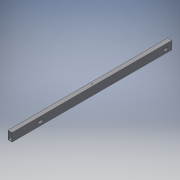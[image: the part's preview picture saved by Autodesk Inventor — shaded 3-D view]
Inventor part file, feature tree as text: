
AUTODESK INVENTOR PART (.ipt)
format: ipt  version: 2018.3 (Build 223284000, 284)  size: 175,616 bytes
history: native  units: in
note: dims shown in document units (in); Inventor stores cm internally (conversion verified against a paired STEP export)
features: extrude x7, sketch x7
ambient origin geometry x8: Origin, YZ Plane, XZ Plane, XY Plane, X Axis, Y Axis, Z Axis, Center Point
bodies: Solid1 (feature_tree)
feature tree (14):
  extrude  "Extrusion1"  Depth=2.0in
  extrude  "Extrusion2"  Depth=0.125in TaperAngle=0.0deg
  extrude  "Extrusion3"  Depth=0.5in TaperAngle=0.0deg
  extrude  "Extrusion7"  Depth=7.0in
  extrude  "Extrusion9"  Depth=1.0in TaperAngle=0.0deg
  extrude  "Extrusion10"  Depth=1.0in
  extrude  "Extrusion11"  Depth=0.5in
  sketch  "Sketch1"  dims[d0=1.0in d1=2.0in]
  sketch  "Sketch2"  dims[d2=0.125in d3=38.5in d4=0.0in]
  sketch  "Sketch3"  dims[d5=1.0in d7=0.5in d8=0.0in]
  sketch  "Sketch7"  dims[d9=1.125in d10=7.0in]
  sketch  "Sketch9"  dims[d11=1.125in d12=1.0in d13=0.0in]
  sketch  "Sketch10"  dims[d34=1.0in d35=1.0in]
  sketch  "Sketch11"  dims[d36=0.5in d37=0.0in d44=0.9375in d45=0.2031in d46=0.2031in d47=0.2031in d48=0.2031in d49=1.0in d50=0.0in d51=0.125in d52=2.0in d53=1.0in d54=0.125in d55=0.125in d56=2.0in d57=1.0in d58=0.125in d59=0.5in d60=0.0in d61=20.0in d62=90.0deg d63=0.2031in d64=4.0in d65=0.0in]
